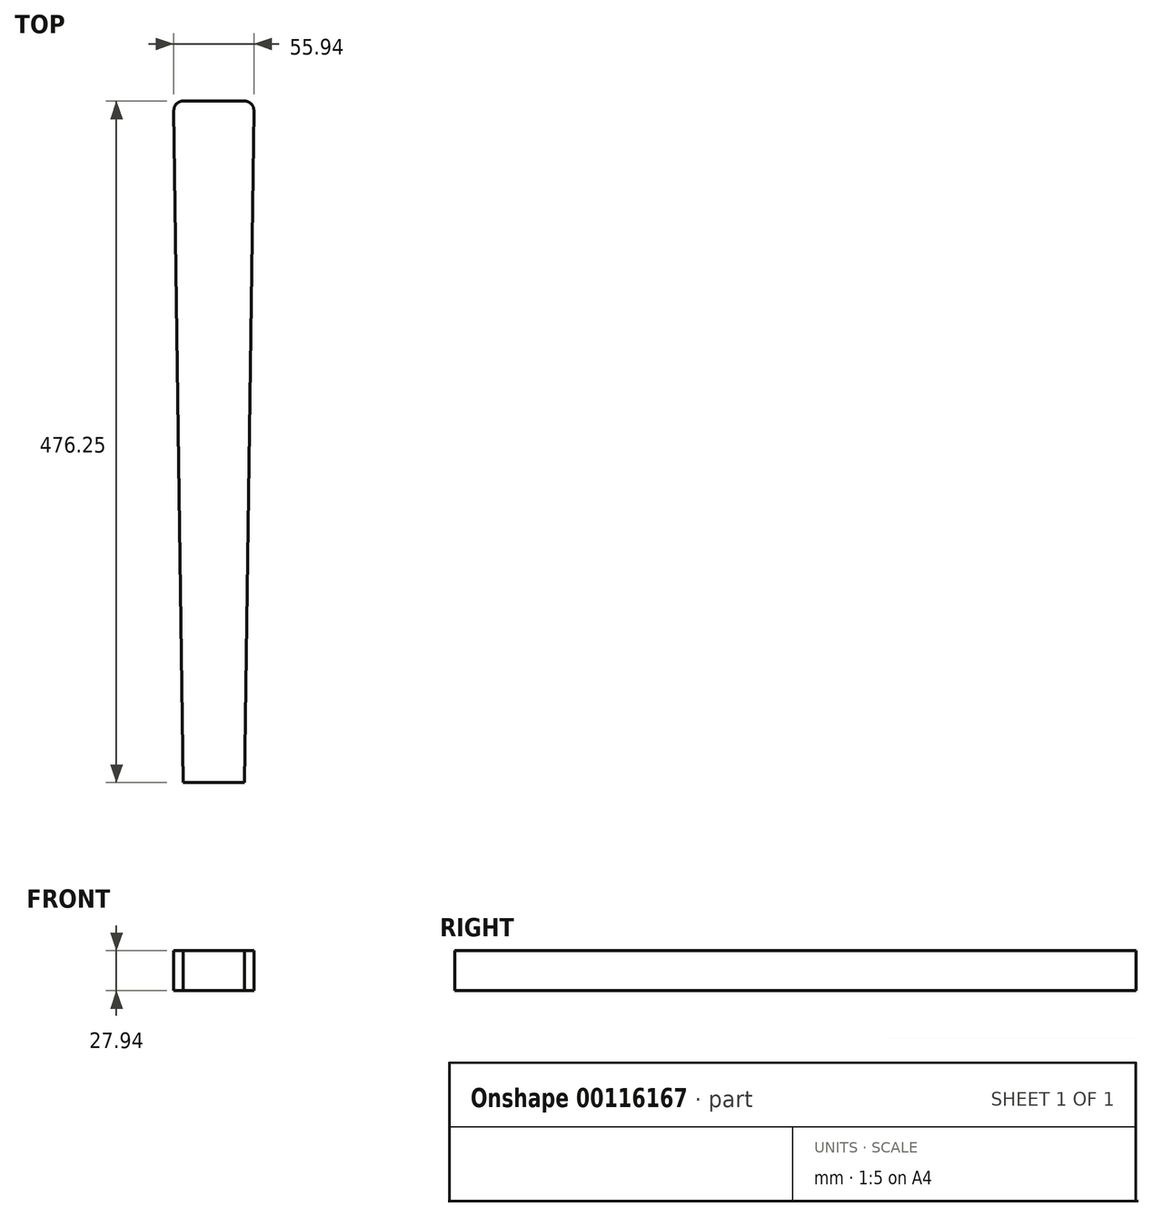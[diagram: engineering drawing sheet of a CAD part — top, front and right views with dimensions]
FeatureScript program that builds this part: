
annotation { "Feature Type Name" : "Feature", "Feature Type Description" : "" }
export const myFeature = defineFeature(function(context is Context, id is Id, definition is map)
    precondition{}
    {
        {
            var Q0;
            Q0=qCreatedBy(makeId("Front.planeOp"),FACE);
            var sketch = newSketch(context, id + "F0", { "sketchPlane" : qUnion([Q0])});
            skLineSegment(sketch, "E0.bottom", {"start": v(-28.05, 13.97) * mm, "end": v(28.05, 13.97) * mm});
            skLineSegment(sketch, "E0.top", {"start": v(-28.05, -13.97) * mm, "end": v(28.05, -13.97) * mm});
            skLineSegment(sketch, "E0.left", {"start": v(-28.05, 13.97) * mm, "end": v(-28.05, -13.97) * mm});
            skLineSegment(sketch, "E0.right", {"start": v(28.05, 13.97) * mm, "end": v(28.05, -13.97) * mm});
            skPoint(sketch, "E0.middle", {"position": v(0, 0) * mm});
            skSolve(sketch);
        }
        {
            var Q0;
            Q0=makeQuery(id+"F0.imprint","IMPRINT",FACE,{"disambiguationData":[TD([[makeQuery(id+"F0.imprint","IMPRINT",EDGE,{"derivedFrom":sQuery(id+"F0.wireOp",EDGE,"E0.bottom")}),-1.0]])]});
            cPlane(context, id + "F1", {"entities" : qUnion([Q0]), "cplaneType" : CPlaneType.OFFSET, "offset" : 476.25 * mm, "width" : 152.4 * mm, "height" : 152.4 * mm});
        }
        {
            var Q0;
            Q0=qCreatedBy(id+"F1.planeOp",FACE);
            var sketch = newSketch(context, id + "F2", { "sketchPlane" : qUnion([Q0])});
            skLineSegment(sketch, "E1.bottom", {"start": v(21.43, -13.97) * mm, "end": v(-21.43, -13.97) * mm});
            skLineSegment(sketch, "E1.top", {"start": v(21.43, 13.97) * mm, "end": v(-21.43, 13.97) * mm});
            skLineSegment(sketch, "E1.left", {"start": v(21.43, -13.97) * mm, "end": v(21.43, 13.97) * mm});
            skLineSegment(sketch, "E1.right", {"start": v(-21.43, -13.97) * mm, "end": v(-21.43, 13.97) * mm});
            skPoint(sketch, "E1.middle", {"position": v(0, 0) * mm});
            skSolve(sketch);
        }
        {
            var Q0;
            Q0=makeQuery(id+"F2.imprint","IMPRINT",FACE,{"disambiguationData":[TD([[makeQuery(id+"F2.imprint","IMPRINT",EDGE,{"derivedFrom":sQuery(id+"F2.wireOp",EDGE,"E1.bottom")}),-1.0]])]});
            var Q1;
            Q1=makeQuery(id+"F0.imprint","IMPRINT",FACE,{"disambiguationData":[TD([[makeQuery(id+"F0.imprint","IMPRINT",EDGE,{"derivedFrom":sQuery(id+"F0.wireOp",EDGE,"E0.bottom")}),-1.0]])]});
            loft(context, id + "F3", {"sheetProfilesArray" : [{ "sheetProfileEntities" : qUnion([Q0]) }, { "sheetProfileEntities" : qUnion([Q1]) }]});
        }
        {
            var Q0;
            Q0=makeQuery(id+"F3.opLoft","MID_CAP_EDGE",EDGE,{"disambiguationData":[OSD([sQuery(id+"F0.wireOp",EDGE,"E0.bottom"),sQuery(id+"F0.wireOp",EDGE,"E0.top"),sQuery(id+"F0.wireOp",EDGE,"E0.left")])],"capPos":1.0});
            var Q1;
            Q1=makeQuery(id+"F3.opLoft","MID_CAP_EDGE",EDGE,{"disambiguationData":[OSD([sQuery(id+"F0.wireOp",EDGE,"E0.bottom"),sQuery(id+"F0.wireOp",EDGE,"E0.top"),sQuery(id+"F0.wireOp",EDGE,"E0.right")])],"capPos":1.0});
            fillet(context, id + "F4", {"entities" : qUnion([Q0, Q1]), "radius" : 6.35 * mm, "tangentPropagation" : true, "allowEdgeOverflow" : false});
        }
    });
